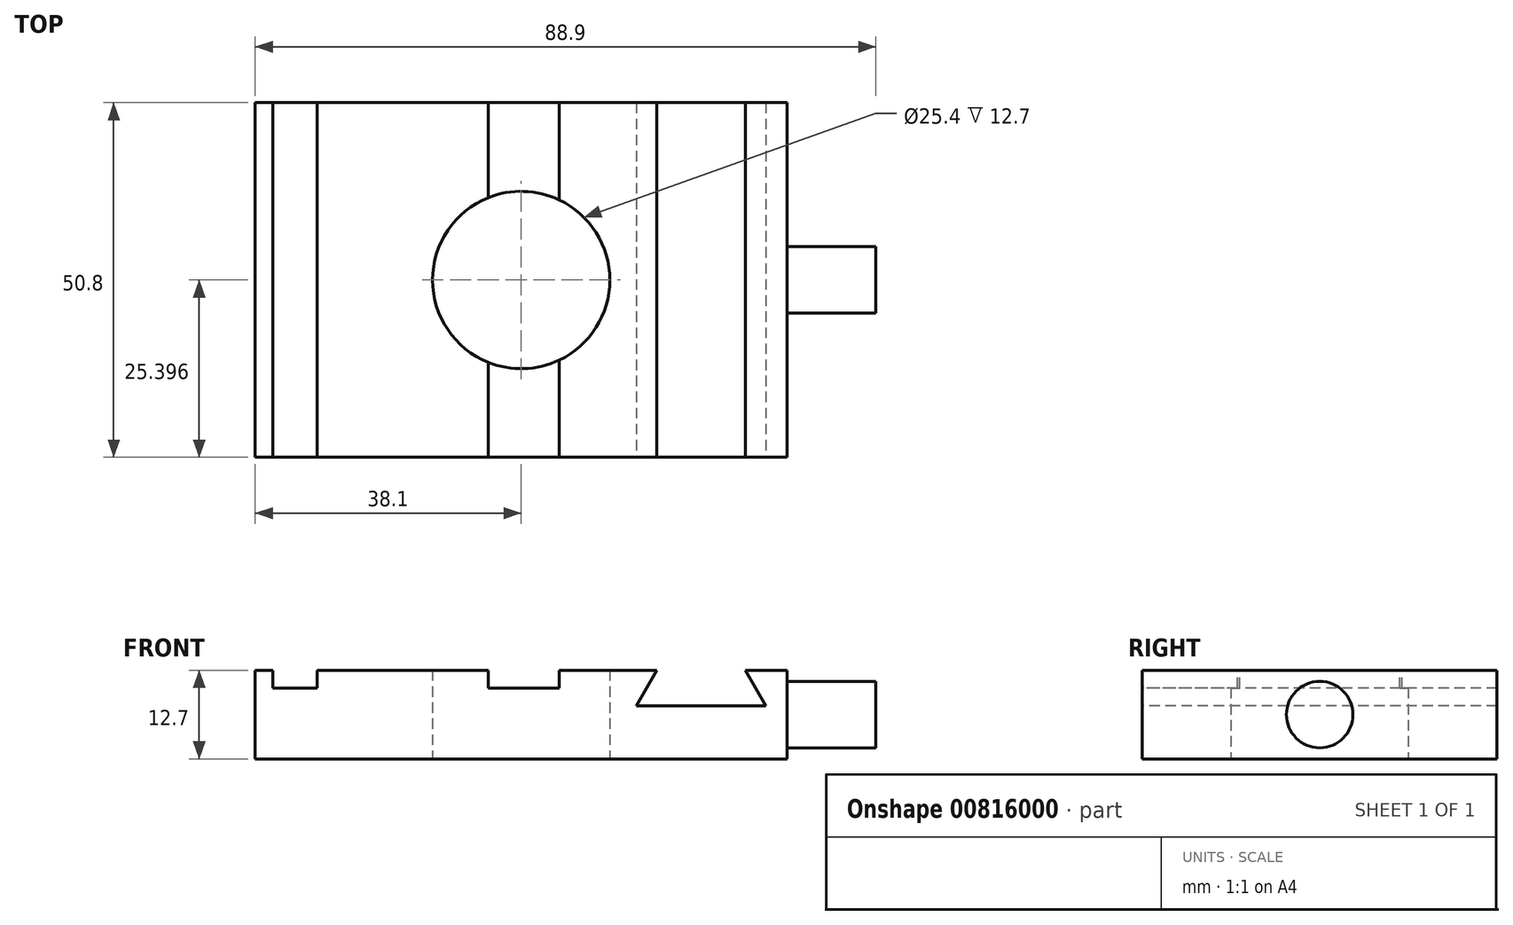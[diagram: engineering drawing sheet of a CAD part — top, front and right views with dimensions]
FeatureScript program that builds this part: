
annotation { "Feature Type Name" : "Feature", "Feature Type Description" : "" }
export const myFeature = defineFeature(function(context is Context, id is Id, definition is map)
    precondition{}
    {
        {
            var Q0;
            Q0=qCreatedBy(makeId("Top.planeOp"),FACE);
            var sketch = newSketch(context, id + "F0", { "sketchPlane" : qUnion([Q0])});
            skLineSegment(sketch, "E0.bottom", {"start": v(38.1, 27.92) * mm, "end": v(-38.1, 27.92) * mm});
            skLineSegment(sketch, "E0.top", {"start": v(38.1, -22.88) * mm, "end": v(-38.1, -22.88) * mm});
            skLineSegment(sketch, "E0.left", {"start": v(38.1, 27.92) * mm, "end": v(38.1, -22.88) * mm});
            skLineSegment(sketch, "E0.right", {"start": v(-38.1, 27.92) * mm, "end": v(-38.1, -22.88) * mm});
            skPoint(sketch, "E0.middle", {"position": v(0, 2.52) * mm});
            skCircle(sketch, "E1", {"center": v(0, 2.52) * mm, "radius": 12.7 * mm});
            skSolve(sketch);
        }
        {
            var Q0;
            Q0=makeQuery(id+"F0.imprint","IMPRINT",FACE,{"disambiguationData":[TD([[makeQuery(id+"F0.imprint","IMPRINT",EDGE,{"derivedFrom":sQuery(id+"F0.wireOp",EDGE,"E0.bottom")}),1.0]])]});
            extrude(context, id + "F1", {"entities" : qUnion([Q0]), "depth" : 12.7 * mm, "offsetDistance" : 25 * mm});
        }
        {
            var Q0;
            Q0=makeQuery(id+"F1.opExtrude","CAP_FACE",FACE,{"disambiguationData":[OSD([sQuery(id+"F0.wireOp",EDGE,"E0.bottom"),sQuery(id+"F0.wireOp",EDGE,"E0.top"),sQuery(id+"F0.wireOp",EDGE,"E0.left"),sQuery(id+"F0.wireOp",EDGE,"E0.right"),sQuery(id+"F0.wireOp",EDGE,"E1")])],"isStart":false});
            var sketch = newSketch(context, id + "F2", { "sketchPlane" : qUnion([Q0])});
            skLineSegment(sketch, "E2.bottom", {"start": v(-35.56, 27.92) * mm, "end": v(-29.21, 27.92) * mm});
            skLineSegment(sketch, "E2.top", {"start": v(-35.56, -22.88) * mm, "end": v(-29.21, -22.88) * mm});
            skLineSegment(sketch, "E2.left", {"start": v(-35.56, 27.92) * mm, "end": v(-35.56, -22.88) * mm});
            skLineSegment(sketch, "E2.right", {"start": v(-29.21, 27.92) * mm, "end": v(-29.21, -22.88) * mm});
            skLineSegment(sketch, "E3", {"start": v(-4.73, 27.92) * mm, "end": v(-4.73, -22.88) * mm});
            skLineSegment(sketch, "E4", {"start": v(5.43, 27.92) * mm, "end": v(5.43, -22.88) * mm});
            skPoint(sketch, "E5", {"position": v(0, 2.52) * mm});
            skLineSegment(sketch, "E6", {"start": v(0, 27.92) * mm, "end": v(0, -22.88) * mm, "construction": true});
            skSolve(sketch);
        }
        {
            var Q0;
            Q0=makeQuery(id+"F2.imprint","IMPRINT",FACE,{"disambiguationData":[TD([[makeQuery(id+"F2.imprint","IMPRINT",EDGE,{"derivedFrom":sQuery(id+"F2.wireOp",EDGE,"E2.bottom")}),1.0]])]});
            var Q1;
            {var subQ0=sQuery(id+"F2.wireOp",EDGE,"E3");var subQ1=makeQuery(id+"F1.opExtrude","CAP_EDGE",EDGE,{"disambiguationData":[OSD([sQuery(id+"F0.wireOp",EDGE,"E0.bottom")])],"isStart":false});var subQ2=makeQuery(id+"F2.imprint","INTERSECT",VERTEX,{"derivedFrom":[subQ1,subQ0]});Q1=makeQuery(id+"F2.imprint","IMPRINT",FACE,{"disambiguationData":[TD([[makeQuery(id+"F2.imprint","IMPRINT",EDGE,{"disambiguationData":[TD([[subQ2,-1.0]])],"derivedFrom":subQ0}),1.0]])]});}
            var Q2;
            {var subQ0=sQuery(id+"F2.wireOp",EDGE,"E3");var subQ1=makeQuery(id+"F1.opExtrude","CAP_EDGE",EDGE,{"disambiguationData":[OSD([sQuery(id+"F0.wireOp",EDGE,"E0.top")])],"isStart":false});var subQ2=makeQuery(id+"F2.imprint","INTERSECT",VERTEX,{"derivedFrom":[subQ1,subQ0]});Q2=makeQuery(id+"F2.imprint","IMPRINT",FACE,{"disambiguationData":[TD([[makeQuery(id+"F2.imprint","IMPRINT",EDGE,{"disambiguationData":[TD([[subQ2,1.0]])],"derivedFrom":subQ0}),1.0]])]});}
            extrude(context, id + "F3", {"entities" : qUnion([Q0, Q1, Q2]), "operationType" : NewBodyOperationType.REMOVE, "oppositeDirection" : true, "depth" : 2.54 * mm, "offsetDistance" : 25.4 * mm});
        }
        {
            var Q0;
            Q0=makeQuery(id+"F1.opExtrude","SWEPT_FACE",FACE,{"disambiguationData":[OSD([sQuery(id+"F0.wireOp",EDGE,"E0.top")])]});
            var sketch = newSketch(context, id + "F4", { "sketchPlane" : qUnion([Q0])});
            skLineSegment(sketch, "E7", {"start": v(19.4, 12.7) * mm, "end": v(16.47, 7.62) * mm});
            skLineSegment(sketch, "E8", {"start": v(16.47, 7.62) * mm, "end": v(35.04, 7.62) * mm});
            skLineSegment(sketch, "E9", {"start": v(35.04, 7.62) * mm, "end": v(32.1, 12.7) * mm});
            skLineSegment(sketch, "E10", {"start": v(32.1, 12.7) * mm, "end": v(19.4, 12.7) * mm});
            skLineSegment(sketch, "E11", {"start": v(25.75, 7.62) * mm, "end": v(25.75, 7.62) * mm});
            skPoint(sketch, "E11.endSnap0", {"position": v(25.75, 12.7) * mm});
            skLineSegment(sketch, "E12", {"start": v(25.75, 7.62) * mm, "end": v(25.75, 12.7) * mm, "construction": true});
            skSolve(sketch);
        }
        {
            var Q0;
            Q0=makeQuery(id+"F4.imprint","IMPRINT",FACE,{"disambiguationData":[TD([[makeQuery(id+"F4.imprint","IMPRINT",EDGE,{"derivedFrom":sQuery(id+"F4.wireOp",EDGE,"E7")}),1.0]])]});
            extrude(context, id + "F5", {"entities" : qUnion([Q0]), "operationType" : NewBodyOperationType.REMOVE, "endBound" : BoundingType.THROUGH_ALL, "oppositeDirection" : true, "depth" : 25.4 * mm, "offsetDistance" : 25.4 * mm});
        }
        {
            var Q0;
            Q0=makeQuery(id+"F1.opExtrude","SWEPT_FACE",FACE,{"disambiguationData":[OSD([sQuery(id+"F0.wireOp",EDGE,"E0.left")])]});
            var sketch = newSketch(context, id + "F6", { "sketchPlane" : qUnion([Q0])});
            skCircle(sketch, "E13", {"center": v(2.52, 6.35) * mm, "radius": 4.76 * mm});
            skPoint(sketch, "E13.centerSnap0", {"position": v(-22.88, 6.35) * mm});
            skPoint(sketch, "E13.centerSnap1", {"position": v(2.52, 12.7) * mm});
            skSolve(sketch);
        }
        {
            var Q0;
            Q0=makeQuery(id+"F6.imprint","IMPRINT",FACE,{"disambiguationData":[TD([[makeQuery(id+"F6.imprint","IMPRINT",EDGE,{"derivedFrom":sQuery(id+"F6.wireOp",EDGE,"E13")}),1.0]])]});
            extrude(context, id + "F7", {"entities" : qUnion([Q0]), "operationType" : NewBodyOperationType.ADD, "depth" : 12.7 * mm, "offsetDistance" : 25.4 * mm});
        }
    });
